# Revit family: DC_Rheem_PLM_MPE06
name_source: partatom
category: Plumbing Fixtures
units: mm (PartAtom-declared; Revit-internal decimal feet)

## family parameters
Cut with Voids When Loaded = No
Host = Face
Part Type = Normal
Room Calculation Point = No
Round Connector Dimension = Use Radius
Shared = No

## types (12) — shared parameters
ColdWaterPipeDiameter_ANZRS = 40 mm  [stored 0.131234 ft]
ColdWaterPipeRadius_ANZRS = 20 mm  [stored 0.0656168 ft]
GasPipeDiameter_ANZRS = 40 mm  [stored 0.131234 ft]
GasPipeRadius_ANZRS = 20 mm  [stored 0.0656168 ft]
HexWidth_ANZRS = 2140 mm  [stored 7.021 ft]
HotWaterPipeDiameter_ANZRS = 40 mm  [stored 0.131234 ft]
HotWaterPipeRadius_ANZRS = 20 mm  [stored 0.0656168 ft]
Manufacturer = Rheem
Materials_ANZRS = Rheem - Stainless Steel
StandWidth_ANZRS = 2060 mm  [stored 6.75853 ft]
Type Comments = 81L/min @ 50°C rise
URL = http://www.rheem.com.au
Width1_ANZRS = 1440 mm  [stored 4.72441 ft]
zero-valued in all types: Default Elevation

## per-type parameters (varying)
| type | Model |
| Multipak - Gas Continuous Flow- Outdoor - 1230 MJ/h Natural gas wall mount - dead leg 60°C + | MPE06N0 |
| Multipak - Gas Continuous Flow- Outdoor - 1230 MJ/h Natural gas wall mount - recirculation 60°C + | MPE06N0/R |
| Multipak - Gas Continuous Flow- Outdoor - 1230 MJ/h Natural gas wall mount - dead leg 50°C | MPE06N0/50 |
| Multipak - Gas Continuous Flow- Outdoor - 1230 MJ/h Natural gas free standing frame - dead leg 60°C + | MPE06NK |
| Multipak - Gas Continuous Flow- Outdoor - 1230 MJ/h Natural gas free standing frame - recirculation 60°C + | MPE06NK/R |
| Multipak - Gas Continuous Flow- Outdoor - 1230 MJ/h Natural gas free standing frame - dead leg 50°C | MPE06NK/50 |
| Multipak - Gas Continuous Flow- Outdoor - 1230 MJ/h Propane gas wall mount - dead leg 60°C + | MPE06P0 |
| Multipak - Gas Continuous Flow- Outdoor - 1230 MJ/h Propane gas wall mount - recirculation 60°C + | MPE06P0/R |
| Multipak - Gas Continuous Flow- Outdoor - 1230 MJ/h Propane gas wall mount - dead leg 50°C | MPE06P0/50 |
| Multipak - Gas Continuous Flow- Outdoor - 1230 MJ/h Propane gas free standing frame - dead leg 60°C + | MPE06PK |
| Multipak - Gas Continuous Flow- Outdoor - 1230 MJ/h Propane gas free standing frame - recirculation 60°C + | MPE06PK/R |
| Multipak - Gas Continuous Flow- Outdoor - 1230 MJ/h Propane gas free standing frame - dead leg 50°C | MPE06PK/50 |

note: column(s) folded — value = type name in every type: Description

note: [stored X ft] marks values corroborated as IEEE doubles in the binary element streams (Revit-internal decimal feet)

## geometry (parser evidence)
native form markers: Blend x12, Sweep x7
no freeform markers — native parametric forms only
